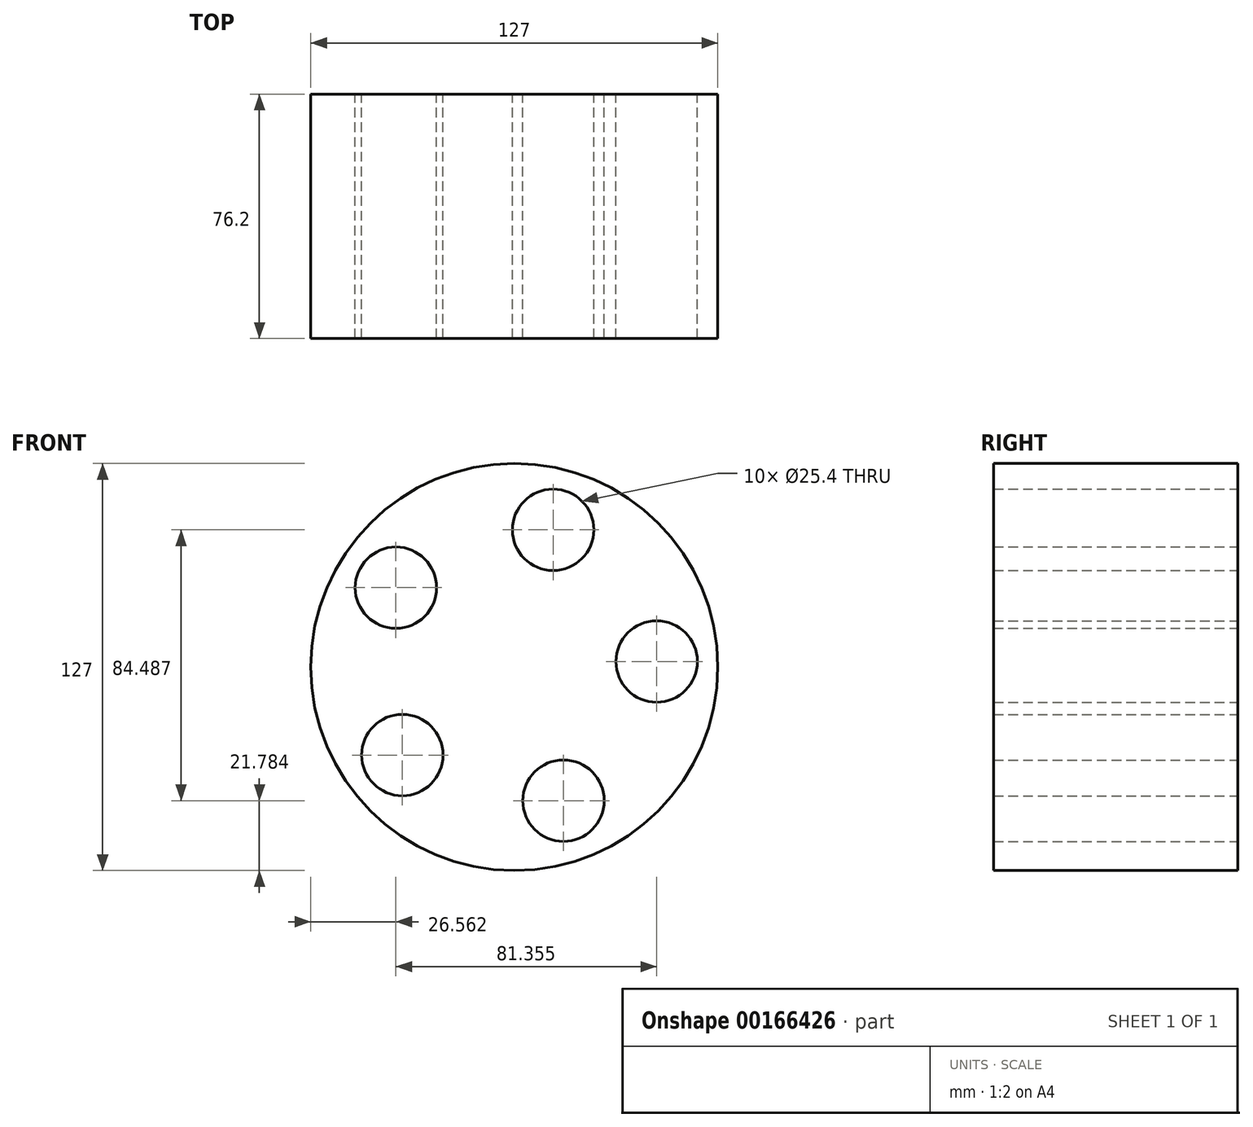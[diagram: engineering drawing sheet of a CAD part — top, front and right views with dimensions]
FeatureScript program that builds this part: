
annotation { "Feature Type Name" : "Feature", "Feature Type Description" : "" }
export const myFeature = defineFeature(function(context is Context, id is Id, definition is map)
    precondition{}
    {
        {
            var Q0;
            Q0=qCreatedBy(makeId("Front.planeOp"),FACE);
            var sketch = newSketch(context, id + "F0", { "sketchPlane" : qUnion([Q0])});
            skCircle(sketch, "E0", {"center": v(0, 0) * mm, "radius": 63.5 * mm});
            skPoint(sketch, "E1", {"position": v(12.1, 42.77) * mm});
            skPoint(sketch, "E2", {"position": v(-36.94, 24.73) * mm});
            skPoint(sketch, "E3", {"position": v(-34.93, -27.49) * mm});
            skPoint(sketch, "E4", {"position": v(15.35, -41.72) * mm});
            skPoint(sketch, "E5", {"position": v(44.42, 1.7) * mm});
            skCircle(sketch, "E6", {"center": v(12.1, 42.77) * mm, "radius": 12.7 * mm});
            skCircle(sketch, "E7", {"center": v(44.42, 1.7) * mm, "radius": 12.7 * mm});
            skCircle(sketch, "E8", {"center": v(15.35, -41.72) * mm, "radius": 12.7 * mm});
            skCircle(sketch, "E9", {"center": v(-34.93, -27.49) * mm, "radius": 12.7 * mm});
            skCircle(sketch, "E10", {"center": v(-36.94, 24.73) * mm, "radius": 12.7 * mm});
            skSolve(sketch);
        }
        {
            var Q0;
            Q0 = qSketchRegion(id + "F0", true);
            extrude(context, id + "F1", {"entities" : qUnion([Q0]), "endBound" : BoundingType.SYMMETRIC, "depth" : 76.2 * mm});
        }
    });
